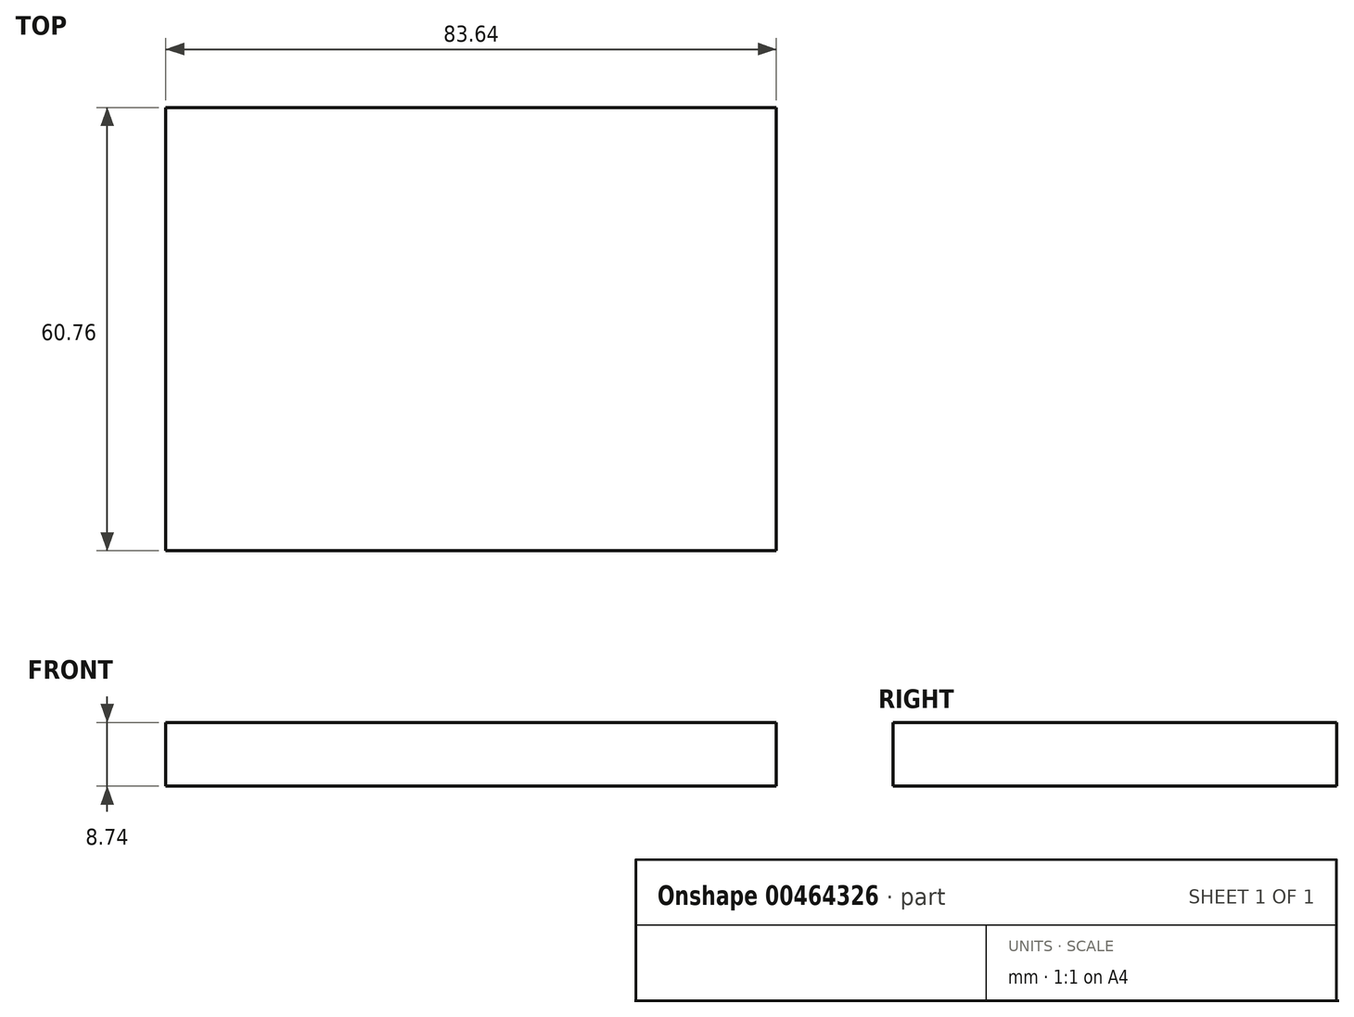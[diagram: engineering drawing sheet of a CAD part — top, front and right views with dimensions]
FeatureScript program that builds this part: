
annotation { "Feature Type Name" : "Feature", "Feature Type Description" : "" }
export const myFeature = defineFeature(function(context is Context, id is Id, definition is map)
    precondition{}
    {
        {
            var Q0;
            Q0=qCreatedBy(makeId("Top.planeOp"),FACE);
            var sketch = newSketch(context, id + "F0", { "sketchPlane" : qUnion([Q0])});
            skLineSegment(sketch, "E0.bottom", {"start": v(41.82, -30.38) * mm, "end": v(-41.82, -30.38) * mm});
            skLineSegment(sketch, "E0.top", {"start": v(41.82, 30.38) * mm, "end": v(-41.82, 30.38) * mm});
            skLineSegment(sketch, "E0.left", {"start": v(41.82, -30.38) * mm, "end": v(41.82, 30.38) * mm});
            skLineSegment(sketch, "E0.right", {"start": v(-41.82, -30.38) * mm, "end": v(-41.82, 30.38) * mm});
            skPoint(sketch, "E0.middle", {"position": v(0, 0) * mm});
            skSolve(sketch);
        }
        {
            var Q0;
            Q0=makeQuery(id+"F0.imprint","IMPRINT",FACE,{"disambiguationData":[TD([[makeQuery(id+"F0.imprint","IMPRINT",EDGE,{"derivedFrom":sQuery(id+"F0.wireOp",EDGE,"E0.bottom")}),-1.0]])]});
            extrude(context, id + "F1", {"entities" : qUnion([Q0]), "depth" : 8.74 * mm});
        }
    });
